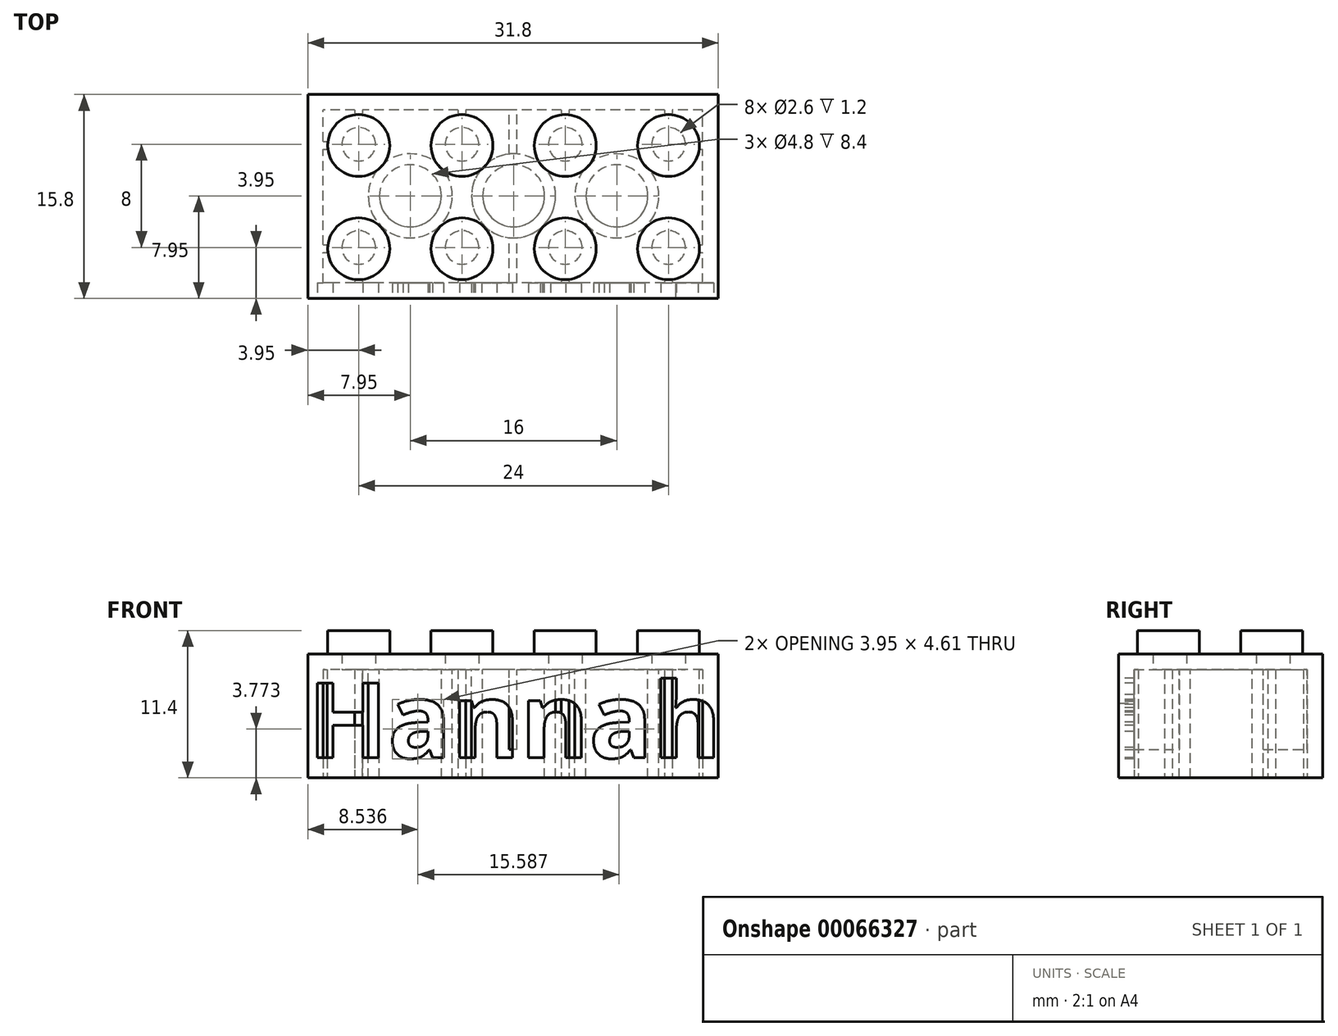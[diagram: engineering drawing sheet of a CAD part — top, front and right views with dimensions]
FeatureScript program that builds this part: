
annotation { "Feature Type Name" : "Feature", "Feature Type Description" : "" }
export const myFeature = defineFeature(function(context is Context, id is Id, definition is map)
    precondition{}
    {
        {
            var Q0;
            Q0=qCreatedBy(makeId("Top.planeOp"),FACE);
            var sketch = newSketch(context, id + "F0", { "sketchPlane" : qUnion([Q0])});
            skLineSegment(sketch, "E0.rect.bottom", {"start": v(15.9, 7.9) * mm, "end": v(-15.9, 7.9) * mm});
            skLineSegment(sketch, "E0.rect.top", {"start": v(15.9, -7.9) * mm, "end": v(-15.9, -7.9) * mm});
            skLineSegment(sketch, "E0.rect.left", {"start": v(15.9, 7.9) * mm, "end": v(15.9, -7.9) * mm});
            skLineSegment(sketch, "E0.rect.right", {"start": v(-15.9, 7.9) * mm, "end": v(-15.9, -7.9) * mm});
            skPoint(sketch, "E0.rect.middle", {"position": v(0, 0) * mm});
            skPoint(sketch, "E1.rect.middle", {"position": v(6.75, -7.9) * mm});
            skSolve(sketch);
        }
        {
            var Q0;
            Q0 = qSketchRegion(id + "F0", true);
            extrude(context, id + "F1", {"entities" : qUnion([Q0]), "depth" : 9.6 * mm});
        }
        {
            var Q0;
            Q0=makeQuery(id+"F1.opExtrude","CAP_FACE",FACE,{"disambiguationData":[OSD([sQuery(id+"F0.wireOp",EDGE,"E0.rect.bottom"),sQuery(id+"F0.wireOp",EDGE,"E0.rect.top"),sQuery(id+"F0.wireOp",EDGE,"E0.rect.left"),sQuery(id+"F0.wireOp",EDGE,"E0.rect.right")])],"isStart":true});
            var sketch = newSketch(context, id + "F2", { "sketchPlane" : qUnion([Q0])});
            skLineSegment(sketch, "E2.rect.bottom", {"start": v(14.7, 6.7) * mm, "end": v(-14.7, 6.7) * mm});
            skLineSegment(sketch, "E2.rect.top", {"start": v(14.7, -6.7) * mm, "end": v(-14.7, -6.7) * mm});
            skLineSegment(sketch, "E2.rect.left", {"start": v(14.7, 6.7) * mm, "end": v(14.7, -6.7) * mm});
            skLineSegment(sketch, "E2.rect.right", {"start": v(-14.7, 6.7) * mm, "end": v(-14.7, -6.7) * mm});
            skPoint(sketch, "E2.rect.middle", {"position": v(0, 0) * mm});
            skSolve(sketch);
        }
        {
            var Q0;
            Q0 = qSketchRegion(id + "F2", true);
            extrude(context, id + "F3", {"entities" : qUnion([Q0]), "operationType" : NewBodyOperationType.REMOVE, "oppositeDirection" : true, "depth" : 8.4 * mm});
        }
        {
            var Q0;
            Q0=makeQuery(id+"F1.opExtrude","CAP_FACE",FACE,{"disambiguationData":[OSD([sQuery(id+"F0.wireOp",EDGE,"E0.rect.bottom"),sQuery(id+"F0.wireOp",EDGE,"E0.rect.top"),sQuery(id+"F0.wireOp",EDGE,"E0.rect.left"),sQuery(id+"F0.wireOp",EDGE,"E0.rect.right")])],"isStart":false});
            var sketch = newSketch(context, id + "F4", { "sketchPlane" : qUnion([Q0])});
            skLineSegment(sketch, "E3", {"start": v(-18.92, 0) * mm, "end": v(20.5, 0) * mm, "construction": true});
            skCircle(sketch, "E4", {"center": v(-11.95, 3.95) * mm, "radius": 2.4 * mm});
            skCircle(sketch, "E5.0.1.0", {"center": v(-11.95, -4.05) * mm, "radius": 2.4 * mm});
            skCircle(sketch, "E5.1.0.0", {"center": v(-3.95, 3.95) * mm, "radius": 2.4 * mm});
            skCircle(sketch, "E5.1.1.0", {"center": v(-3.95, -4.05) * mm, "radius": 2.4 * mm});
            skCircle(sketch, "E5.2.0.0", {"center": v(4.05, 3.95) * mm, "radius": 2.4 * mm});
            skCircle(sketch, "E5.2.1.0", {"center": v(4.05, -4.05) * mm, "radius": 2.4 * mm});
            skCircle(sketch, "E5.3.0.0", {"center": v(12.05, 3.95) * mm, "radius": 2.4 * mm});
            skCircle(sketch, "E5.3.1.0", {"center": v(12.05, -4.05) * mm, "radius": 2.4 * mm});
            skLineSegment(sketch, "E5.direction1", {"start": v(-11.95, 3.95) * mm, "end": v(-3.95, 3.95) * mm, "construction": true});
            skLineSegment(sketch, "E5.direction2", {"start": v(-11.95, 3.95) * mm, "end": v(-11.95, -4.05) * mm, "construction": true});
            skSolve(sketch);
        }
        {
            var Q0;
            Q0 = qSketchRegion(id + "F4", true);
            extrude(context, id + "F5", {"entities" : qUnion([Q0]), "operationType" : NewBodyOperationType.ADD, "depth" : 1.8 * mm});
        }
        {
            var Q0;
            Q0=makeQuery(id+"F3.boolean.opBoolean","COPY",FACE,{"derivedFrom":makeQuery(id+"F3.opExtrude","CAP_FACE",FACE,{"disambiguationData":[OSD([sQuery(id+"F2.wireOp",EDGE,"E2.rect.bottom"),sQuery(id+"F2.wireOp",EDGE,"E2.rect.top"),sQuery(id+"F2.wireOp",EDGE,"E2.rect.left"),sQuery(id+"F2.wireOp",EDGE,"E2.rect.right")])],"isStart":false})});
            var sketch = newSketch(context, id + "F6", { "sketchPlane" : qUnion([Q0])});
            skCircle(sketch, "E6", {"center": v(-11.95, 3.95) * mm, "radius": 1.3 * mm});
            skCircle(sketch, "E7.0.1.0", {"center": v(-11.95, -4.05) * mm, "radius": 1.3 * mm});
            skCircle(sketch, "E7.1.0.0", {"center": v(-3.95, 3.95) * mm, "radius": 1.3 * mm});
            skCircle(sketch, "E7.1.1.0", {"center": v(-3.95, -4.05) * mm, "radius": 1.3 * mm});
            skCircle(sketch, "E7.2.0.0", {"center": v(4.05, 3.95) * mm, "radius": 1.3 * mm});
            skCircle(sketch, "E7.2.1.0", {"center": v(4.05, -4.05) * mm, "radius": 1.3 * mm});
            skCircle(sketch, "E7.3.0.0", {"center": v(12.05, 3.95) * mm, "radius": 1.3 * mm});
            skCircle(sketch, "E7.3.1.0", {"center": v(12.05, -4.05) * mm, "radius": 1.3 * mm});
            skLineSegment(sketch, "E7.direction1", {"start": v(-11.95, 3.95) * mm, "end": v(-3.95, 3.95) * mm, "construction": true});
            skLineSegment(sketch, "E7.direction2", {"start": v(-11.95, 3.95) * mm, "end": v(-11.95, -4.05) * mm, "construction": true});
            skSolve(sketch);
        }
        {
            var Q0;
            Q0 = qSketchRegion(id + "F6", true);
            extrude(context, id + "F7", {"entities" : qUnion([Q0]), "operationType" : NewBodyOperationType.REMOVE, "oppositeDirection" : true, "depth" : 1.2 * mm});
        }
        {
            var Q0;
            Q0=makeQuery(id+"F3.boolean.opBoolean","COPY",FACE,{"derivedFrom":makeQuery(id+"F3.opExtrude","CAP_FACE",FACE,{"disambiguationData":[OSD([sQuery(id+"F2.wireOp",EDGE,"E2.rect.bottom"),sQuery(id+"F2.wireOp",EDGE,"E2.rect.top"),sQuery(id+"F2.wireOp",EDGE,"E2.rect.left"),sQuery(id+"F2.wireOp",EDGE,"E2.rect.right")])],"isStart":false})});
            var sketch = newSketch(context, id + "F8", { "sketchPlane" : qUnion([Q0])});
            skLineSegment(sketch, "E8", {"start": v(-3.95, 3.95) * mm, "end": v(-11.95, -4.05) * mm, "construction": true});
            skLineSegment(sketch, "E9", {"start": v(4.05, 3.95) * mm, "end": v(-3.95, -4.05) * mm, "construction": true});
            skLineSegment(sketch, "E10", {"start": v(-3.95, 3.95) * mm, "end": v(4.05, -4.05) * mm, "construction": true});
            skLineSegment(sketch, "E11", {"start": v(4.05, -4.05) * mm, "end": v(12.05, 3.95) * mm, "construction": true});
            skLineSegment(sketch, "E12", {"start": v(12.05, -4.05) * mm, "end": v(4.05, 3.95) * mm, "construction": true});
            skLineSegment(sketch, "E13", {"start": v(-11.95, 3.95) * mm, "end": v(-3.95, -4.05) * mm, "construction": true});
            skCircle(sketch, "E14", {"center": v(-7.95, -0.05) * mm, "radius": 2.4 * mm});
            skCircle(sketch, "E15", {"center": v(-7.95, -0.05) * mm, "radius": 3.25 * mm});
            skCircle(sketch, "E16", {"center": v(0.05, -0.05) * mm, "radius": 2.4 * mm});
            skCircle(sketch, "E17", {"center": v(0.05, -0.05) * mm, "radius": 3.25 * mm});
            skCircle(sketch, "E18", {"center": v(8.05, -0.05) * mm, "radius": 2.4 * mm});
            skCircle(sketch, "E19", {"center": v(8.05, -0.05) * mm, "radius": 3.25 * mm});
            skSolve(sketch);
        }
        {
            var Q0;
            Q0 = qSketchRegion(id + "F8", true);
            var Q1;
            Q1=makeQuery(id+"F1.opExtrude","CAP_FACE",FACE,{"disambiguationData":[OSD([sQuery(id+"F0.wireOp",EDGE,"E0.rect.bottom"),sQuery(id+"F0.wireOp",EDGE,"E0.rect.top"),sQuery(id+"F0.wireOp",EDGE,"E0.rect.left"),sQuery(id+"F0.wireOp",EDGE,"E0.rect.right")])],"isStart":true});
            extrude(context, id + "F9", {"entities" : qUnion([Q0]), "operationType" : NewBodyOperationType.ADD, "endBound" : BoundingType.UP_TO_SURFACE, "endBoundEntityFace" : qUnion([Q1]), "depth" : 25 * mm});
        }
        {
            var Q0;
            Q0=makeQuery(id+"F1.opExtrude","CAP_FACE",FACE,{"disambiguationData":[OSD([sQuery(id+"F0.wireOp",EDGE,"E0.rect.bottom"),sQuery(id+"F0.wireOp",EDGE,"E0.rect.top"),sQuery(id+"F0.wireOp",EDGE,"E0.rect.left"),sQuery(id+"F0.wireOp",EDGE,"E0.rect.right")])],"isStart":true});
            var sketch = newSketch(context, id + "F10", { "sketchPlane" : qUnion([Q0])});
            skLineSegment(sketch, "E20.bottom", {"start": v(-12.25, 6.7) * mm, "end": v(-11.65, 6.7) * mm});
            skLineSegment(sketch, "E20.top", {"start": v(-12.25, 6.4) * mm, "end": v(-11.65, 6.4) * mm});
            skLineSegment(sketch, "E20.left", {"start": v(-12.25, 6.7) * mm, "end": v(-12.25, 6.4) * mm});
            skLineSegment(sketch, "E20.right", {"start": v(-11.65, 6.7) * mm, "end": v(-11.65, 6.4) * mm});
            skLineSegment(sketch, "E21", {"start": v(-11.95, -3.95) * mm, "end": v(-11.95, -1.66) * mm, "construction": true});
            skLineSegment(sketch, "E22", {"start": v(-11.95, -3.95) * mm, "end": v(-11.95, 10.15) * mm, "construction": true});
            skLineSegment(sketch, "E23.0.1.0", {"start": v(-11.65, -6.4) * mm, "end": v(-11.65, -6.7) * mm});
            skLineSegment(sketch, "E23.0.1.1", {"start": v(-12.25, -6.4) * mm, "end": v(-11.65, -6.4) * mm});
            skLineSegment(sketch, "E23.0.1.2", {"start": v(-12.25, -6.4) * mm, "end": v(-12.25, -6.7) * mm});
            skLineSegment(sketch, "E23.0.1.3", {"start": v(-12.25, -6.7) * mm, "end": v(-11.65, -6.7) * mm});
            skLineSegment(sketch, "E23.1.0.0", {"start": v(-3.65, 6.7) * mm, "end": v(-3.65, 6.4) * mm});
            skLineSegment(sketch, "E23.1.0.1", {"start": v(-4.25, 6.7) * mm, "end": v(-3.65, 6.7) * mm});
            skLineSegment(sketch, "E23.1.0.2", {"start": v(-4.25, 6.7) * mm, "end": v(-4.25, 6.4) * mm});
            skLineSegment(sketch, "E23.1.0.3", {"start": v(-4.25, 6.4) * mm, "end": v(-3.65, 6.4) * mm});
            skLineSegment(sketch, "E23.1.1.0", {"start": v(-3.65, -6.4) * mm, "end": v(-3.65, -6.7) * mm});
            skLineSegment(sketch, "E23.1.1.1", {"start": v(-4.25, -6.4) * mm, "end": v(-3.65, -6.4) * mm});
            skLineSegment(sketch, "E23.1.1.2", {"start": v(-4.25, -6.4) * mm, "end": v(-4.25, -6.7) * mm});
            skLineSegment(sketch, "E23.1.1.3", {"start": v(-4.25, -6.7) * mm, "end": v(-3.65, -6.7) * mm});
            skLineSegment(sketch, "E23.2.0.0", {"start": v(4.35, 6.7) * mm, "end": v(4.35, 6.4) * mm});
            skLineSegment(sketch, "E23.2.0.1", {"start": v(3.75, 6.7) * mm, "end": v(4.35, 6.7) * mm});
            skLineSegment(sketch, "E23.2.0.2", {"start": v(3.75, 6.7) * mm, "end": v(3.75, 6.4) * mm});
            skLineSegment(sketch, "E23.2.0.3", {"start": v(3.75, 6.4) * mm, "end": v(4.35, 6.4) * mm});
            skLineSegment(sketch, "E23.2.1.0", {"start": v(4.35, -6.4) * mm, "end": v(4.35, -6.7) * mm});
            skLineSegment(sketch, "E23.2.1.1", {"start": v(3.75, -6.4) * mm, "end": v(4.35, -6.4) * mm});
            skLineSegment(sketch, "E23.2.1.2", {"start": v(3.75, -6.4) * mm, "end": v(3.75, -6.7) * mm});
            skLineSegment(sketch, "E23.2.1.3", {"start": v(3.75, -6.7) * mm, "end": v(4.35, -6.7) * mm});
            skLineSegment(sketch, "E23.3.0.0", {"start": v(12.35, 6.7) * mm, "end": v(12.35, 6.4) * mm});
            skLineSegment(sketch, "E23.3.0.1", {"start": v(11.75, 6.7) * mm, "end": v(12.35, 6.7) * mm});
            skLineSegment(sketch, "E23.3.0.2", {"start": v(11.75, 6.7) * mm, "end": v(11.75, 6.4) * mm});
            skLineSegment(sketch, "E23.3.0.3", {"start": v(11.75, 6.4) * mm, "end": v(12.35, 6.4) * mm});
            skLineSegment(sketch, "E23.3.1.0", {"start": v(12.35, -6.4) * mm, "end": v(12.35, -6.7) * mm});
            skLineSegment(sketch, "E23.3.1.1", {"start": v(11.75, -6.4) * mm, "end": v(12.35, -6.4) * mm});
            skLineSegment(sketch, "E23.3.1.2", {"start": v(11.75, -6.4) * mm, "end": v(11.75, -6.7) * mm});
            skLineSegment(sketch, "E23.3.1.3", {"start": v(11.75, -6.7) * mm, "end": v(12.35, -6.7) * mm});
            skLineSegment(sketch, "E23.direction1", {"start": v(-11.65, 6.4) * mm, "end": v(-3.65, 6.4) * mm, "construction": true});
            skLineSegment(sketch, "E23.direction2", {"start": v(-11.65, 6.4) * mm, "end": v(-11.65, -6.7) * mm, "construction": true});
            skSolve(sketch);
        }
        {
            var Q0;
            Q0 = qSketchRegion(id + "F10", true);
            var Q1;
            {var subQ0=sQuery(id+"F2.wireOp",EDGE,"E2.rect.bottom");var subQ1=sQuery(id+"F2.wireOp",EDGE,"E2.rect.top");var subQ2=sQuery(id+"F2.wireOp",EDGE,"E2.rect.left");var subQ3=sQuery(id+"F2.wireOp",EDGE,"E2.rect.right");Q1=makeQuery(id+"F9.boolean.opBoolean","SPLIT",FACE,{"disambiguationData":[TD([makeQuery(id+"F3.boolean.opBoolean","COPY",FACE,{"derivedFrom":makeQuery(id+"F3.opExtrude","SWEPT_FACE",FACE,{"disambiguationData":[OSD([subQ0])]})})])],"derivedFrom":makeQuery(id+"F3.boolean.opBoolean","COPY",FACE,{"derivedFrom":makeQuery(id+"F3.opExtrude","CAP_FACE",FACE,{"disambiguationData":[OSD([subQ0,subQ1,subQ2,subQ3])],"isStart":false})})});}
            extrude(context, id + "F11", {"entities" : qUnion([Q0]), "operationType" : NewBodyOperationType.ADD, "endBound" : BoundingType.UP_TO_SURFACE, "oppositeDirection" : true, "endBoundEntityFace" : qUnion([Q1]), "depth" : 25 * mm});
        }
        {
            var Q0;
            Q0=makeQuery(id+"F11.boolean.opBoolean","MERGE",FACE,{"derivedFrom":[makeQuery(id+"F1.opExtrude","CAP_FACE",FACE,{"disambiguationData":[OSD([sQuery(id+"F0.wireOp",EDGE,"E0.rect.bottom"),sQuery(id+"F0.wireOp",EDGE,"E0.rect.top"),sQuery(id+"F0.wireOp",EDGE,"E0.rect.left"),sQuery(id+"F0.wireOp",EDGE,"E0.rect.right")])],"isStart":true}),makeQuery(id+"F11.opExtrude","CAP_FACE",FACE,{"disambiguationData":[OSD([sQuery(id+"F10.wireOp",EDGE,"E20.bottom"),sQuery(id+"F10.wireOp",EDGE,"E20.top"),sQuery(id+"F10.wireOp",EDGE,"E20.left"),sQuery(id+"F10.wireOp",EDGE,"E20.right")])],"isStart":true}),makeQuery(id+"F11.opExtrude","CAP_FACE",FACE,{"disambiguationData":[OSD([sQuery(id+"F10.wireOp",EDGE,"E23.0.1.0"),sQuery(id+"F10.wireOp",EDGE,"E23.0.1.1"),sQuery(id+"F10.wireOp",EDGE,"E23.0.1.2"),sQuery(id+"F10.wireOp",EDGE,"E23.0.1.3")])],"isStart":true}),makeQuery(id+"F11.opExtrude","CAP_FACE",FACE,{"disambiguationData":[OSD([sQuery(id+"F10.wireOp",EDGE,"E23.1.0.0"),sQuery(id+"F10.wireOp",EDGE,"E23.1.0.1"),sQuery(id+"F10.wireOp",EDGE,"E23.1.0.2"),sQuery(id+"F10.wireOp",EDGE,"E23.1.0.3")])],"isStart":true}),makeQuery(id+"F11.opExtrude","CAP_FACE",FACE,{"disambiguationData":[OSD([sQuery(id+"F10.wireOp",EDGE,"E23.1.1.0"),sQuery(id+"F10.wireOp",EDGE,"E23.1.1.1"),sQuery(id+"F10.wireOp",EDGE,"E23.1.1.2"),sQuery(id+"F10.wireOp",EDGE,"E23.1.1.3")])],"isStart":true}),makeQuery(id+"F11.opExtrude","CAP_FACE",FACE,{"disambiguationData":[OSD([sQuery(id+"F10.wireOp",EDGE,"E23.2.0.0"),sQuery(id+"F10.wireOp",EDGE,"E23.2.0.1"),sQuery(id+"F10.wireOp",EDGE,"E23.2.0.2"),sQuery(id+"F10.wireOp",EDGE,"E23.2.0.3")])],"isStart":true}),makeQuery(id+"F11.opExtrude","CAP_FACE",FACE,{"disambiguationData":[OSD([sQuery(id+"F10.wireOp",EDGE,"E23.2.1.0"),sQuery(id+"F10.wireOp",EDGE,"E23.2.1.1"),sQuery(id+"F10.wireOp",EDGE,"E23.2.1.2"),sQuery(id+"F10.wireOp",EDGE,"E23.2.1.3")])],"isStart":true}),makeQuery(id+"F11.opExtrude","CAP_FACE",FACE,{"disambiguationData":[OSD([sQuery(id+"F10.wireOp",EDGE,"E23.3.0.0"),sQuery(id+"F10.wireOp",EDGE,"E23.3.0.1"),sQuery(id+"F10.wireOp",EDGE,"E23.3.0.2"),sQuery(id+"F10.wireOp",EDGE,"E23.3.0.3")])],"isStart":true}),makeQuery(id+"F11.opExtrude","CAP_FACE",FACE,{"disambiguationData":[OSD([sQuery(id+"F10.wireOp",EDGE,"E23.3.1.0"),sQuery(id+"F10.wireOp",EDGE,"E23.3.1.1"),sQuery(id+"F10.wireOp",EDGE,"E23.3.1.2"),sQuery(id+"F10.wireOp",EDGE,"E23.3.1.3")])],"isStart":true})]});
            var sketch = newSketch(context, id + "F12", { "sketchPlane" : qUnion([Q0])});
            skLineSegment(sketch, "E24", {"start": v(-17.6, -3.95) * mm, "end": v(-11.95, -3.95) * mm, "construction": true});
            skLineSegment(sketch, "E25.bottom", {"start": v(-14.4, -4.25) * mm, "end": v(-14.7, -4.25) * mm});
            skLineSegment(sketch, "E25.top", {"start": v(-14.4, -3.65) * mm, "end": v(-14.7, -3.65) * mm});
            skLineSegment(sketch, "E25.left", {"start": v(-14.4, -4.25) * mm, "end": v(-14.4, -3.65) * mm});
            skLineSegment(sketch, "E25.right", {"start": v(-14.7, -4.25) * mm, "end": v(-14.7, -3.65) * mm});
            skLineSegment(sketch, "E26.0.1.0", {"start": v(-14.4, 4.35) * mm, "end": v(-14.7, 4.35) * mm});
            skLineSegment(sketch, "E26.0.1.1", {"start": v(-14.4, 3.75) * mm, "end": v(-14.4, 4.35) * mm});
            skLineSegment(sketch, "E26.0.1.2", {"start": v(-14.4, 3.75) * mm, "end": v(-14.7, 3.75) * mm});
            skLineSegment(sketch, "E26.0.1.3", {"start": v(-14.7, 3.75) * mm, "end": v(-14.7, 4.35) * mm});
            skLineSegment(sketch, "E26.1.0.0", {"start": v(14.7, -3.65) * mm, "end": v(14.4, -3.65) * mm});
            skLineSegment(sketch, "E26.1.0.1", {"start": v(14.7, -4.25) * mm, "end": v(14.7, -3.65) * mm});
            skLineSegment(sketch, "E26.1.0.2", {"start": v(14.7, -4.25) * mm, "end": v(14.4, -4.25) * mm});
            skLineSegment(sketch, "E26.1.0.3", {"start": v(14.4, -4.25) * mm, "end": v(14.4, -3.65) * mm});
            skLineSegment(sketch, "E26.1.1.0", {"start": v(14.7, 4.35) * mm, "end": v(14.4, 4.35) * mm});
            skLineSegment(sketch, "E26.1.1.1", {"start": v(14.7, 3.75) * mm, "end": v(14.7, 4.35) * mm});
            skLineSegment(sketch, "E26.1.1.2", {"start": v(14.7, 3.75) * mm, "end": v(14.4, 3.75) * mm});
            skLineSegment(sketch, "E26.1.1.3", {"start": v(14.4, 3.75) * mm, "end": v(14.4, 4.35) * mm});
            skLineSegment(sketch, "E26.direction1", {"start": v(-14.7, -3.65) * mm, "end": v(14.4, -3.65) * mm, "construction": true});
            skLineSegment(sketch, "E26.direction2", {"start": v(-14.7, -3.65) * mm, "end": v(-14.7, 4.35) * mm, "construction": true});
            skSolve(sketch);
        }
        {
            var Q0;
            Q0 = qSketchRegion(id + "F12", true);
            var Q1;
            {var subQ0=sQuery(id+"F2.wireOp",EDGE,"E2.rect.bottom");var subQ1=sQuery(id+"F2.wireOp",EDGE,"E2.rect.top");var subQ2=sQuery(id+"F2.wireOp",EDGE,"E2.rect.left");var subQ3=sQuery(id+"F2.wireOp",EDGE,"E2.rect.right");Q1=makeQuery(id+"F9.boolean.opBoolean","SPLIT",FACE,{"disambiguationData":[TD([makeQuery(id+"F3.boolean.opBoolean","COPY",FACE,{"derivedFrom":makeQuery(id+"F3.opExtrude","SWEPT_FACE",FACE,{"disambiguationData":[OSD([subQ0])]})})])],"derivedFrom":makeQuery(id+"F3.boolean.opBoolean","COPY",FACE,{"derivedFrom":makeQuery(id+"F3.opExtrude","CAP_FACE",FACE,{"disambiguationData":[OSD([subQ0,subQ1,subQ2,subQ3])],"isStart":false})})});}
            extrude(context, id + "F13", {"entities" : qUnion([Q0]), "operationType" : NewBodyOperationType.ADD, "endBound" : BoundingType.UP_TO_SURFACE, "oppositeDirection" : true, "endBoundEntityFace" : qUnion([Q1]), "depth" : 25 * mm});
        }
        {
            var Q0;
            {var subQ0=sQuery(id+"F2.wireOp",EDGE,"E2.rect.bottom");var subQ1=sQuery(id+"F2.wireOp",EDGE,"E2.rect.top");var subQ2=sQuery(id+"F2.wireOp",EDGE,"E2.rect.left");var subQ3=sQuery(id+"F2.wireOp",EDGE,"E2.rect.right");Q0=makeQuery(id+"F9.boolean.opBoolean","SPLIT",FACE,{"disambiguationData":[TD([makeQuery(id+"F3.boolean.opBoolean","COPY",FACE,{"derivedFrom":makeQuery(id+"F3.opExtrude","SWEPT_FACE",FACE,{"disambiguationData":[OSD([subQ0])]})})])],"derivedFrom":makeQuery(id+"F3.boolean.opBoolean","COPY",FACE,{"derivedFrom":makeQuery(id+"F3.opExtrude","CAP_FACE",FACE,{"disambiguationData":[OSD([subQ0,subQ1,subQ2,subQ3])],"isStart":false})})});}
            var sketch = newSketch(context, id + "F14", { "sketchPlane" : qUnion([Q0])});
            skLineSegment(sketch, "E27.bottom", {"start": v(-0.3, -2.7) * mm, "end": v(0.3, -2.7) * mm});
            skLineSegment(sketch, "E27.top", {"start": v(-0.3, -6.7) * mm, "end": v(0.3, -6.7) * mm});
            skLineSegment(sketch, "E27.left", {"start": v(-0.3, -2.7) * mm, "end": v(-0.3, -6.7) * mm});
            skLineSegment(sketch, "E27.right", {"start": v(0.3, -2.7) * mm, "end": v(0.3, -6.7) * mm});
            skSolve(sketch);
        }
        {
            var Q0;
            Q0 = qSketchRegion(id + "F14", true);
            extrude(context, id + "F15", {"entities" : qUnion([Q0]), "operationType" : NewBodyOperationType.ADD, "depth" : 6.2 * mm});
        }
        {
            var Q0;
            {var subQ0=sQuery(id+"F2.wireOp",EDGE,"E2.rect.bottom");var subQ1=sQuery(id+"F2.wireOp",EDGE,"E2.rect.top");var subQ2=sQuery(id+"F2.wireOp",EDGE,"E2.rect.left");var subQ3=sQuery(id+"F2.wireOp",EDGE,"E2.rect.right");Q0=makeQuery(id+"F9.boolean.opBoolean","SPLIT",FACE,{"disambiguationData":[TD([makeQuery(id+"F3.boolean.opBoolean","COPY",FACE,{"derivedFrom":makeQuery(id+"F3.opExtrude","SWEPT_FACE",FACE,{"disambiguationData":[OSD([subQ0])]})})])],"derivedFrom":makeQuery(id+"F3.boolean.opBoolean","COPY",FACE,{"derivedFrom":makeQuery(id+"F3.opExtrude","CAP_FACE",FACE,{"disambiguationData":[OSD([subQ0,subQ1,subQ2,subQ3])],"isStart":false})})});}
            var sketch = newSketch(context, id + "F16", { "sketchPlane" : qUnion([Q0])});
            skLineSegment(sketch, "E28.bottom", {"start": v(-0.3, 6.7) * mm, "end": v(0.3, 6.7) * mm});
            skLineSegment(sketch, "E28.top", {"start": v(-0.3, 2.7) * mm, "end": v(0.3, 2.7) * mm});
            skLineSegment(sketch, "E28.left", {"start": v(-0.3, 6.7) * mm, "end": v(-0.3, 2.7) * mm});
            skLineSegment(sketch, "E28.right", {"start": v(0.3, 6.7) * mm, "end": v(0.3, 2.7) * mm});
            skSolve(sketch);
        }
        {
            var Q0;
            Q0 = qSketchRegion(id + "F16", true);
            extrude(context, id + "F17", {"entities" : qUnion([Q0]), "operationType" : NewBodyOperationType.ADD, "depth" : 6.2 * mm});
        }
        {
            var Q0;
            Q0=makeQuery(id+"F1.opExtrude","SWEPT_FACE",FACE,{"disambiguationData":[OSD([sQuery(id+"F0.wireOp",EDGE,"E0.rect.top")])]});
            var sketch = newSketch(context, id + "F18", { "sketchPlane" : qUnion([Q0])});
            skText(sketch, "E29", { "text": "Hannah\n", "fontName": "OpenSans-Bold.ttf"});
            const initialGuessF18  = {"E29": [-0.0159, 0.00155, 1, 0, 0.00585]};
            skSetInitialGuess(sketch, initialGuessF18);
            skSolve(sketch);
        }
        {
            var Q0;
            Q0 = qSketchRegion(id + "F18", true);
            extrude(context, id + "F19", {"entities" : qUnion([Q0]), "operationType" : NewBodyOperationType.REMOVE, "oppositeDirection" : true, "depth" : 1.2 * mm});
        }
    });
